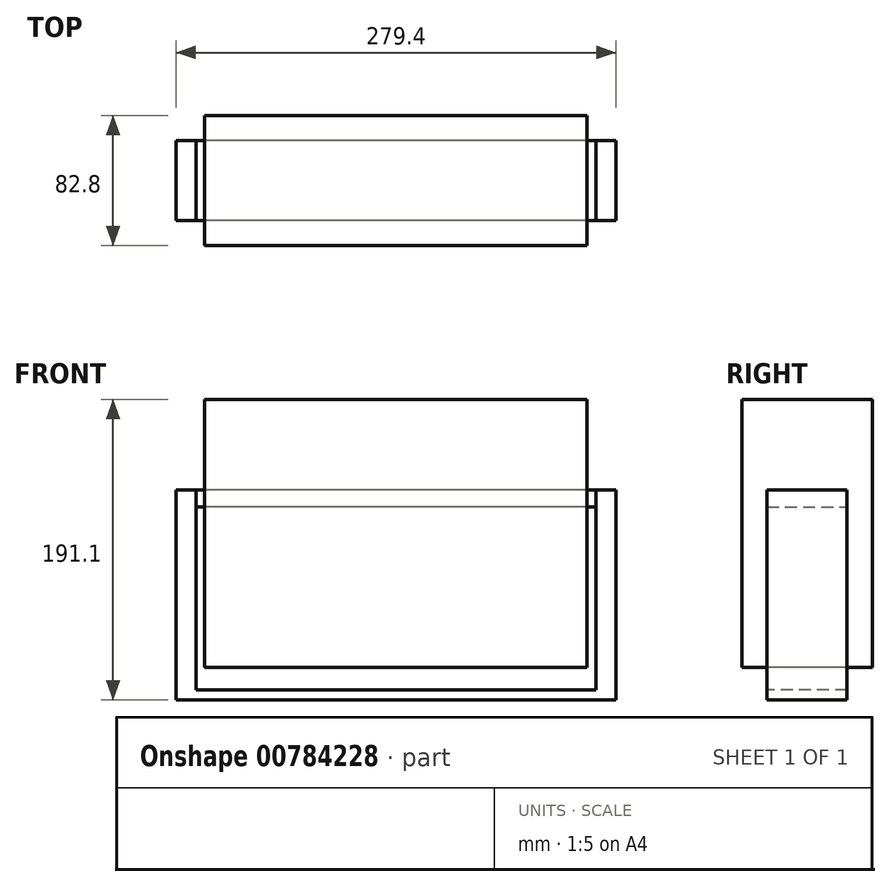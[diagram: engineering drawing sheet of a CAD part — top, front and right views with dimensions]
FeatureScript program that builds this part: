
annotation { "Feature Type Name" : "Feature", "Feature Type Description" : "" }
export const myFeature = defineFeature(function(context is Context, id is Id, definition is map)
    precondition{}
    {
        {
            var Q0;
            Q0=qCreatedBy(makeId("Top.planeOp"),FACE);
            var sketch = newSketch(context, id + "F0", { "sketchPlane" : qUnion([Q0])});
            skLineSegment(sketch, "E0.bottom", {"start": v(-121.41, 54.38) * mm, "end": v(121.41, 54.38) * mm});
            skLineSegment(sketch, "E0.top", {"start": v(-121.41, -28.42) * mm, "end": v(121.41, -28.42) * mm});
            skLineSegment(sketch, "E0.left", {"start": v(-121.41, 54.38) * mm, "end": v(-121.41, -28.42) * mm});
            skLineSegment(sketch, "E0.right", {"start": v(121.41, 54.38) * mm, "end": v(121.41, -28.42) * mm});
            skSolve(sketch);
        }
        {
            var Q0;
            Q0=makeQuery(id+"F0.imprint","IMPRINT",FACE,{"disambiguationData":[TD([[makeQuery(id+"F0.imprint","IMPRINT",EDGE,{"derivedFrom":sQuery(id+"F0.wireOp",EDGE,"E0.bottom")}),-1.0]])]});
            extrude(context, id + "F1", {"entities" : qUnion([Q0]), "depth" : 170.43 * mm, "offsetDistance" : 25.4 * mm});
        }
        {
            var Q0;
            Q0=qCreatedBy(makeId("Right.planeOp"),FACE);
            var sketch = newSketch(context, id + "F2", { "sketchPlane" : qUnion([Q0])});
            skLineSegment(sketch, "E1.bottom", {"start": v(-12.42, -14.32) * mm, "end": v(38.38, -14.32) * mm});
            skLineSegment(sketch, "E1.top", {"start": v(-12.42, -20.67) * mm, "end": v(38.38, -20.67) * mm});
            skLineSegment(sketch, "E1.left", {"start": v(-12.42, -14.32) * mm, "end": v(-12.42, -20.67) * mm});
            skLineSegment(sketch, "E1.right", {"start": v(38.38, -14.32) * mm, "end": v(38.38, -20.67) * mm});
            skSolve(sketch);
        }
        {
            var Q0;
            Q0=makeQuery(id+"F2.imprint","IMPRINT",FACE,{"disambiguationData":[TD([[makeQuery(id+"F2.imprint","IMPRINT",EDGE,{"derivedFrom":sQuery(id+"F2.wireOp",EDGE,"E1.bottom")}),-1.0]])]});
            extrude(context, id + "F3", {"entities" : qUnion([Q0]), "endBound" : BoundingType.SYMMETRIC, "depth" : 279.4 * mm, "offsetDistance" : 25.4 * mm});
        }
        {
            var Q0;
            Q0=makeQuery(id+"F3.opExtrude","SWEPT_FACE",FACE,{"disambiguationData":[OSD([sQuery(id+"F2.wireOp",EDGE,"E1.bottom")])]});
            var sketch = newSketch(context, id + "F4", { "sketchPlane" : qUnion([Q0])});
            skLineSegment(sketch, "E2.bottom", {"start": v(-139.7, 38.38) * mm, "end": v(-127, 38.38) * mm});
            skLineSegment(sketch, "E2.top", {"start": v(-139.7, -12.42) * mm, "end": v(-127, -12.42) * mm});
            skLineSegment(sketch, "E2.left", {"start": v(-139.7, 38.38) * mm, "end": v(-139.7, -12.42) * mm});
            skLineSegment(sketch, "E2.right", {"start": v(-127, 38.38) * mm, "end": v(-127, -12.42) * mm});
            skLineSegment(sketch, "E3.bottom", {"start": v(139.7, 38.38) * mm, "end": v(127, 38.38) * mm});
            skLineSegment(sketch, "E3.top", {"start": v(139.7, -12.42) * mm, "end": v(127, -12.42) * mm});
            skLineSegment(sketch, "E3.left", {"start": v(139.7, 38.38) * mm, "end": v(139.7, -12.42) * mm});
            skLineSegment(sketch, "E3.right", {"start": v(127, 38.38) * mm, "end": v(127, -12.42) * mm});
            skSolve(sketch);
        }
        {
            var Q0;
            Q0=makeQuery(id+"F4.imprint","IMPRINT",FACE,{"disambiguationData":[TD([[makeQuery(id+"F4.imprint","IMPRINT",EDGE,{"derivedFrom":sQuery(id+"F4.wireOp",EDGE,"E2.bottom")}),1.0]])]});
            var Q1;
            Q1=makeQuery(id+"F4.imprint","IMPRINT",FACE,{"disambiguationData":[TD([[makeQuery(id+"F4.imprint","IMPRINT",EDGE,{"derivedFrom":sQuery(id+"F4.wireOp",EDGE,"E3.bottom")}),1.0]])]});
            extrude(context, id + "F5", {"entities" : qUnion([Q0, Q1]), "operationType" : NewBodyOperationType.ADD, "depth" : 127 * mm, "offsetDistance" : 25.4 * mm});
        }
        {
            var Q0;
            Q0=makeQuery(id+"F5.opExtrude","SWEPT_FACE",FACE,{"disambiguationData":[OSD([sQuery(id+"F4.wireOp",EDGE,"E2.right")])]});
            var sketch = newSketch(context, id + "F6", { "sketchPlane" : qUnion([Q0])});
            skLineSegment(sketch, "E4.bottom", {"start": v(-12.42, 112.68) * mm, "end": v(38.38, 112.68) * mm});
            skLineSegment(sketch, "E4.top", {"start": v(-12.42, 102.03) * mm, "end": v(38.38, 102.03) * mm});
            skLineSegment(sketch, "E4.left", {"start": v(-12.42, 112.68) * mm, "end": v(-12.42, 102.03) * mm});
            skLineSegment(sketch, "E4.right", {"start": v(38.38, 112.68) * mm, "end": v(38.38, 102.03) * mm});
            skSolve(sketch);
        }
        {
            var Q0;
            Q0=makeQuery(id+"F6.imprint","IMPRINT",FACE,{"disambiguationData":[TD([[makeQuery(id+"F6.imprint","IMPRINT",EDGE,{"derivedFrom":sQuery(id+"F6.wireOp",EDGE,"E4.bottom")}),1.0]])]});
            extrude(context, id + "F7", {"entities" : qUnion([Q0]), "depth" : 254 * mm, "offsetDistance" : 25.4 * mm});
        }
    });
